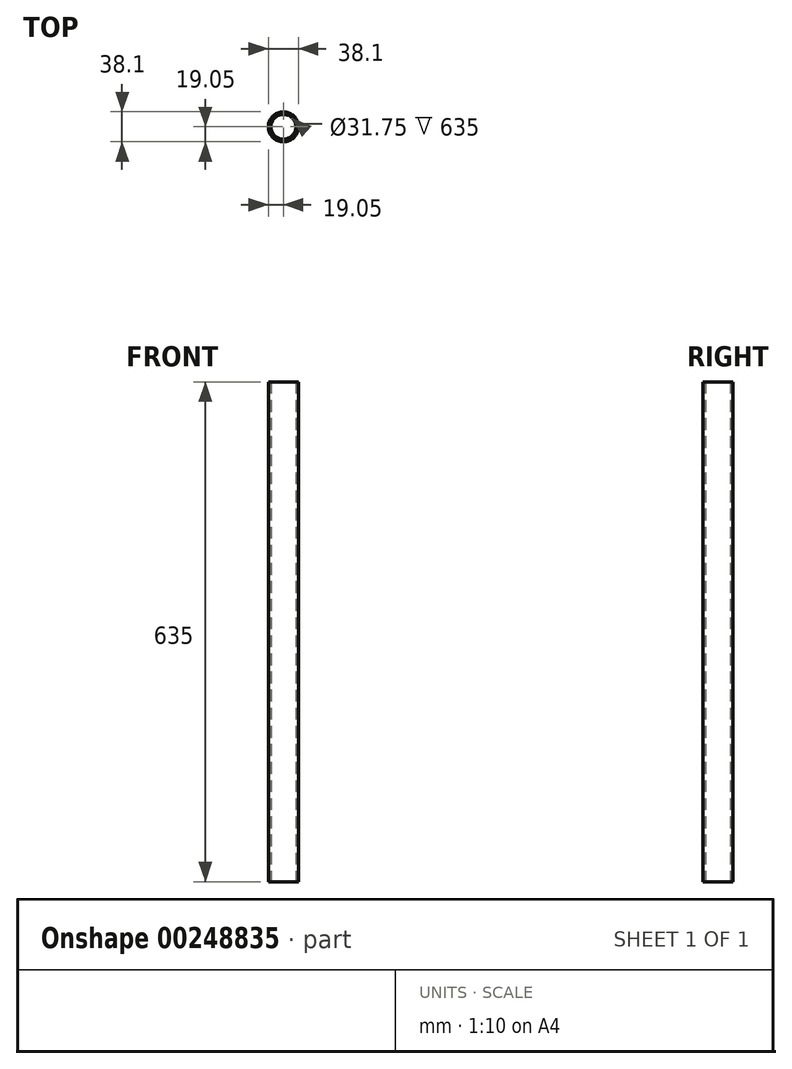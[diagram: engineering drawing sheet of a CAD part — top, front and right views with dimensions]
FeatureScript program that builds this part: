
annotation { "Feature Type Name" : "Feature", "Feature Type Description" : "" }
export const myFeature = defineFeature(function(context is Context, id is Id, definition is map)
    precondition{}
    {
        {
            var Q0;
            Q0=qCreatedBy(makeId("Top.planeOp"),FACE);
            var sketch = newSketch(context, id + "F0", { "sketchPlane" : qUnion([Q0])});
            skCircle(sketch, "E0", {"center": v(0, 0) * mm, "radius": 19.05 * mm});
            skCircle(sketch, "E1", {"center": v(0, 0) * mm, "radius": 15.88 * mm});
            skSolve(sketch);
        }
        {
            var Q0;
            Q0=makeQuery(id+"F0.imprint","IMPRINT",FACE,{"disambiguationData":[TD([[makeQuery(id+"F0.imprint","IMPRINT",EDGE,{"derivedFrom":sQuery(id+"F0.wireOp",EDGE,"E0")}),1.0]])]});
            extrude(context, id + "F1", {"entities" : qUnion([Q0]), "depth" : 635 * mm});
        }
    });
